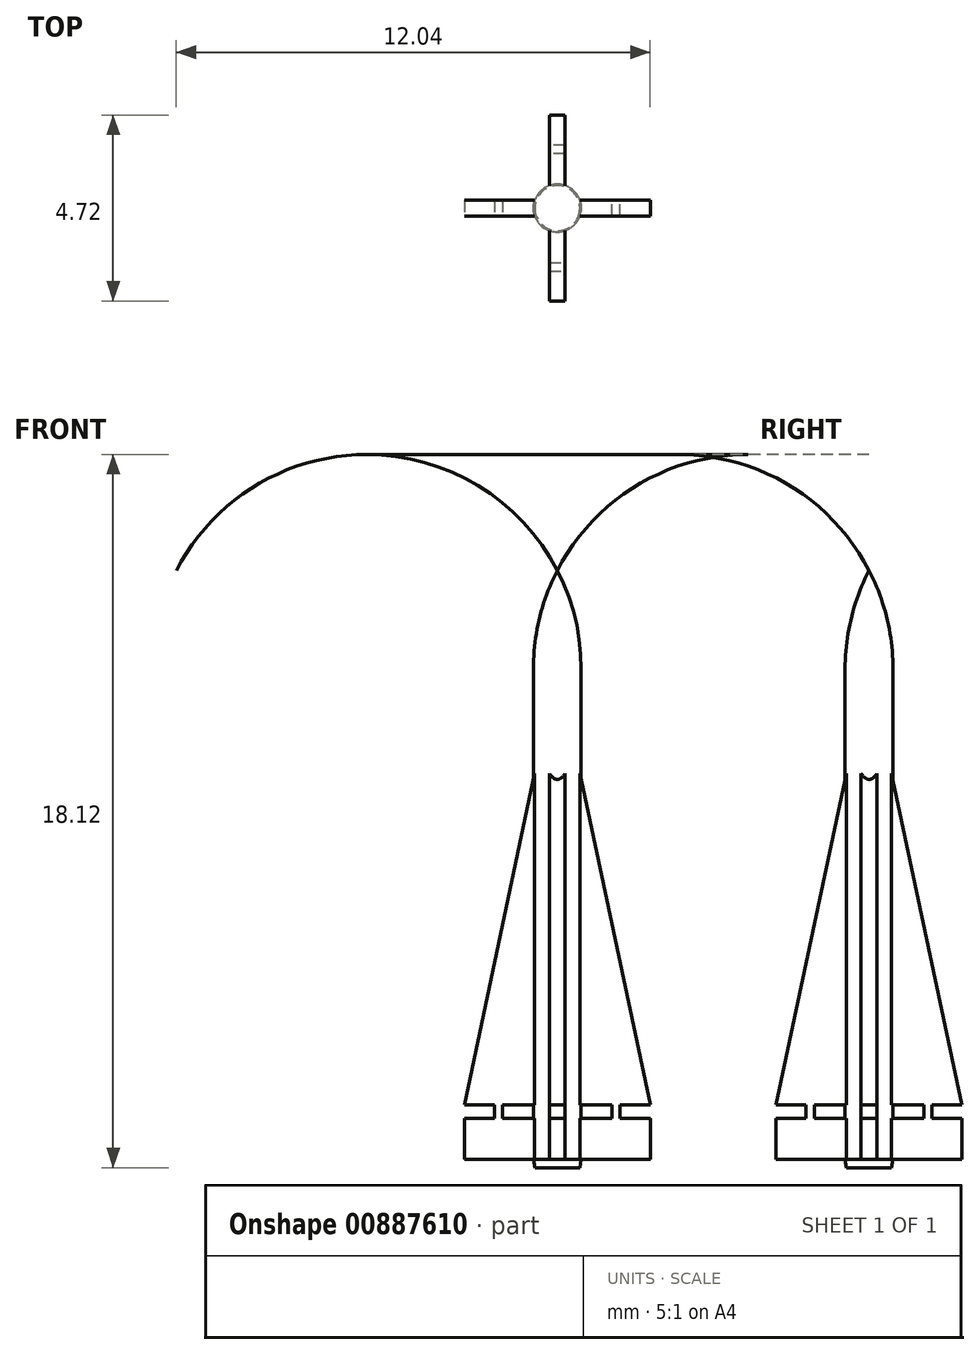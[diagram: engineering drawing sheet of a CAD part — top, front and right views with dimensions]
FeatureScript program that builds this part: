
annotation { "Feature Type Name" : "Feature", "Feature Type Description" : "" }
export const myFeature = defineFeature(function(context is Context, id is Id, definition is map)
    precondition{}
    {
        {
            var Q0;
            Q0=qCreatedBy(makeId("Front.planeOp"),FACE);
            var sketch = newSketch(context, id + "F0", { "sketchPlane" : qUnion([Q0])});
            skLineSegment(sketch, "E0", {"start": v(0, 0) * mm, "end": v(0, 15.17) * mm});
            skLineSegment(sketch, "E1", {"start": v(0.6, 12.67) * mm, "end": v(0.6, 0) * mm});
            skLineSegment(sketch, "E2", {"start": v(0.6, 0) * mm, "end": v(0, 0) * mm});
            skArc(sketch, "E3", {"start": v(0.6, 12.67) * mm, "mid": v(0.45, 13.96) * mm, "end": v(0, 15.17) * mm});
            skLineSegment(sketch, "E4", {"start": v(0.6, 0.2) * mm, "end": v(0.57, 0) * mm});
            skSolve(sketch);
        }
        {
            var Q0;
            {var subQ0=sQuery(id+"F0.wireOp",EDGE,"mrwio9nY-PsAZ-Zbfy-NhIU-sYq0QVbgGXAG");Q0=makeQuery(id+"F0.imprint","IMPRINT",FACE,{"disambiguationData":[TD([[makeQuery(id+"F0.imprint","IMPRINT",EDGE,{"derivedFrom":subQ0}),-1.0]])]});}
            var Q1;
            {var subQ7=sQuery(id+"F0.wireOp",EDGE,"E0");Q1=makeQuery(id+"F0.imprint","IMPRINT",FACE,{"disambiguationData":[TD([[makeQuery(id+"F0.imprint","IMPRINT",EDGE,{"derivedFrom":subQ7}),-1.0]])]});}
            var Q2;
            Q2=sQuery(id+"F0.wireOp",EDGE,"E0");
            revolve(context, id + "F1", {"surfaceOperationType" : NewSurfaceOperationType.NEW, "entities" : qUnion([Q0, Q1]), "axis" : qUnion([Q2]), "revolveType" : RevolveType.FULL});
        }
        {
            var Q0;
            Q0=qCreatedBy(makeId("Front.planeOp"),FACE);
            var sketch = newSketch(context, id + "F2", { "sketchPlane" : qUnion([Q0])});
            skLineSegment(sketch, "E5", {"start": v(0, 0) * mm, "end": v(0, 11.38) * mm});
            skLineSegment(sketch, "E6", {"start": v(0.4, 1.6) * mm, "end": v(0.4, 1.25) * mm});
            skLineSegment(sketch, "E7", {"start": v(0.4, 1.25) * mm, "end": v(2.36, 1.25) * mm});
            skLineSegment(sketch, "E8", {"start": v(0.6, 0) * mm, "end": v(0.6, 32.87) * mm, "construction": true});
            skLineSegment(sketch, "E9", {"start": v(0.4, 1.6) * mm, "end": v(2.36, 1.6) * mm});
            skLineSegment(sketch, "E10", {"start": v(2.36, 1.6) * mm, "end": v(0.29, 11.38) * mm});
            skPoint(sketch, "E11", {"position": v(0.6, 1.6) * mm});
            skLineSegment(sketch, "E12", {"start": v(0, 0.2) * mm, "end": v(2.36, 0.2) * mm});
            skLineSegment(sketch, "E13", {"start": v(2.36, 0.2) * mm, "end": v(2.36, 1.25) * mm});
            skLineSegment(sketch, "E14", {"start": v(1.39, 1.6) * mm, "end": v(1.39, 1.25) * mm});
            skLineSegment(sketch, "E15", {"start": v(1.6, 1.6) * mm, "end": v(1.6, 1.25) * mm});
            skLineSegment(sketch, "E16", {"start": v(0.29, 11.38) * mm, "end": v(0, 11.38) * mm});
            skPoint(sketch, "E17", {"position": v(0.6, 9.86) * mm});
            skLineSegment(sketch, "E18.0", {"start": v(0.6, 0.2) * mm, "end": v(-0.6, 0.2) * mm});
            skSolve(sketch);
        }
        {
            var Q0;
            {var subQ3=sQuery(id+"F2.wireOp",EDGE,"E14");var subQ14=sQuery(id+"F2.wireOp",EDGE,"E6");Q0=qUnion([makeQuery(id+"F2.imprint","IMPRINT",FACE,{"disambiguationData":[TD([[makeQuery(id+"F2.imprint","IMPRINT",EDGE,{"derivedFrom":subQ14}),-1.0]])]}),makeQuery(id+"F2.imprint","IMPRINT",FACE,{"disambiguationData":[TD([[makeQuery(id+"F2.imprint","IMPRINT",EDGE,{"derivedFrom":subQ3}),1.0]])]})]);}
            extrude(context, id + "F3", {"entities" : qUnion([Q0]), "operationType" : NewBodyOperationType.ADD, "depth" : .4 * mm, "offsetDistance" : 25 * mm, "symmetric" : true});
        }
        {
            var Q0;
            Q0=makeQuery(id+"F1.opRevolve","SWEPT_BODY",BODY,{"disambiguationData":[OSD([sQuery(id+"F0.wireOp",EDGE,"E0"),sQuery(id+"F0.wireOp",EDGE,"E1"),sQuery(id+"F0.wireOp",EDGE,"E2"),sQuery(id+"F0.wireOp",EDGE,"2EiOItwe-9FNA-eY8p-DkXH-AMy5AHyUmzZA"),sQuery(id+"F0.wireOp",EDGE,"lF35QjYl-MEgV-fRWE-0Yr6-Bt5vS8A7brRf")])]});
            var Q1;
            Q1=makeQuery(id+"F1.opRevolve","SWEPT_FACE",FACE,{"disambiguationData":[OSD([sQuery(id+"F0.wireOp",EDGE,"E1")])]});
            circularPattern(context, id + "F4", {"operationType" : NewBodyOperationType.ADD, "entities" : qUnion([Q0]), "axis" : qUnion([Q1]), "angle" : 360 * degree, "instanceCount" : 4, "equalSpace" : true, "computeTransformsWithoutBuiltin" : true});
        }
    });
